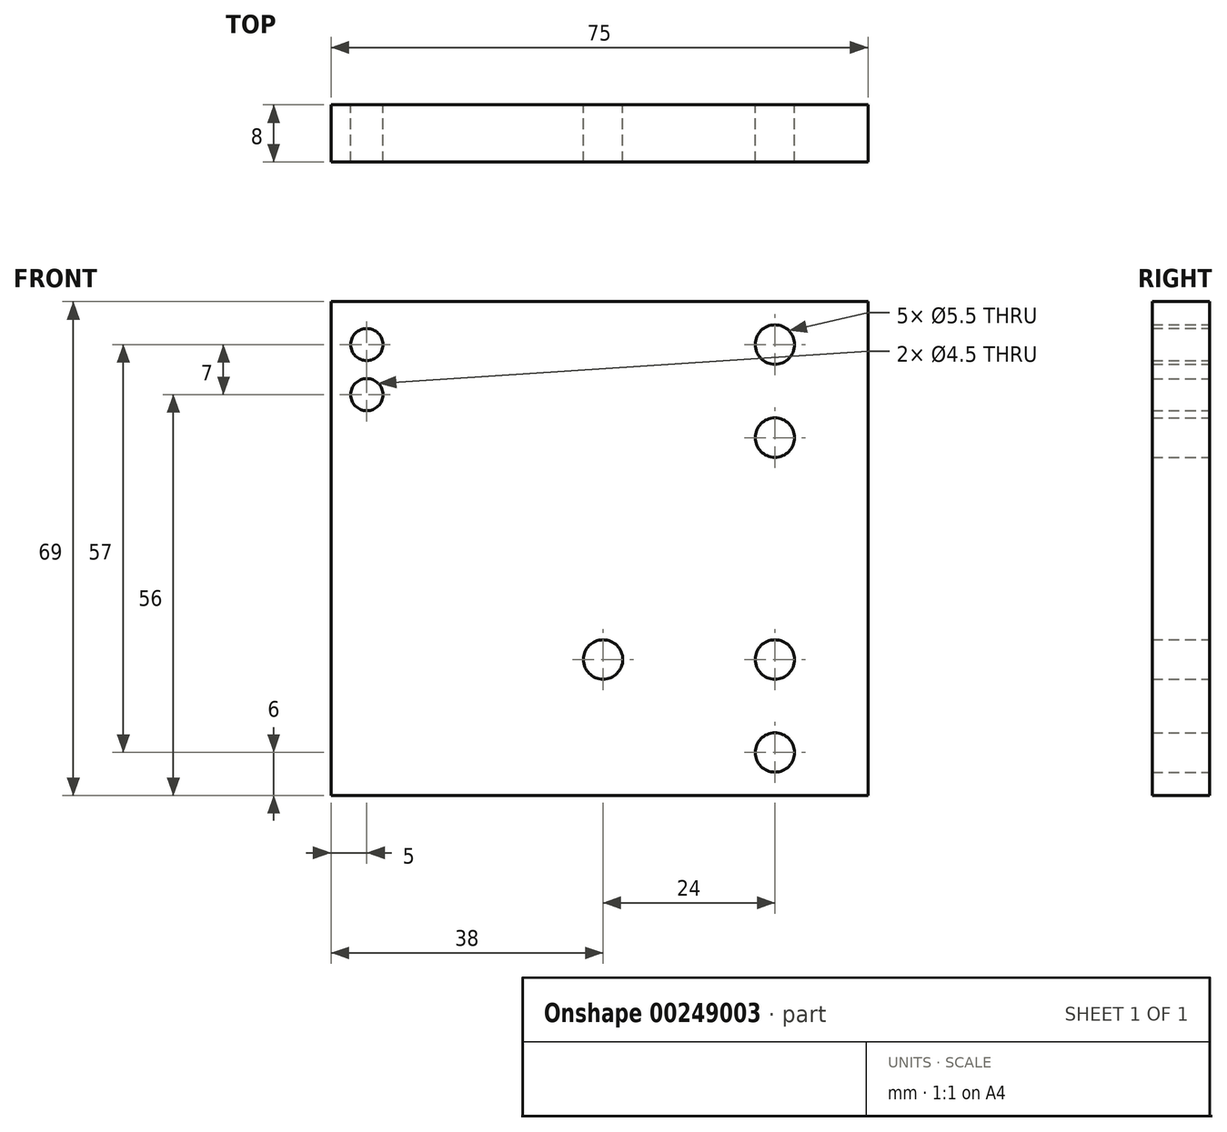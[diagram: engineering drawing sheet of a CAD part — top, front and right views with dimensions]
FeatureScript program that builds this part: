
annotation { "Feature Type Name" : "Feature", "Feature Type Description" : "" }
export const myFeature = defineFeature(function(context is Context, id is Id, definition is map)
    precondition{}
    {
        {
            var Q0;
            Q0=qCreatedBy(makeId("Front.planeOp"),FACE);
            var sketch = newSketch(context, id + "F0", { "sketchPlane" : qUnion([Q0])});
            skLineSegment(sketch, "E0.bottom", {"start": v(37.5, -34.5) * mm, "end": v(-37.5, -34.5) * mm});
            skLineSegment(sketch, "E0.top", {"start": v(37.5, 34.5) * mm, "end": v(-37.5, 34.5) * mm});
            skLineSegment(sketch, "E0.left", {"start": v(37.5, -34.5) * mm, "end": v(37.5, 34.5) * mm});
            skLineSegment(sketch, "E0.right", {"start": v(-37.5, -34.5) * mm, "end": v(-37.5, 34.5) * mm});
            skPoint(sketch, "E0.middle", {"position": v(0, 0) * mm});
            skCircle(sketch, "E1", {"center": v(24.5, -28.5) * mm, "radius": 2.75 * mm});
            skCircle(sketch, "E2", {"center": v(24.5, -15.5) * mm, "radius": 2.75 * mm});
            skCircle(sketch, "E3", {"center": v(24.5, 15.5) * mm, "radius": 2.75 * mm});
            skCircle(sketch, "E4", {"center": v(24.5, 28.5) * mm, "radius": 2.75 * mm});
            skCircle(sketch, "E5", {"center": v(-32.5, 28.5) * mm, "radius": 2.25 * mm});
            skCircle(sketch, "E6", {"center": v(-32.5, 21.5) * mm, "radius": 2.25 * mm});
            skPoint(sketch, "E7", {"position": v(0.5, -15.5) * mm});
            skSolve(sketch);
        }
        {
            var Q0;
            Q0=makeQuery(id+"F0.imprint","IMPRINT",FACE,{"disambiguationData":[TD([[makeQuery(id+"F0.imprint","IMPRINT",EDGE,{"derivedFrom":sQuery(id+"F0.wireOp",EDGE,"E0.bottom")}),-1.0]])]});
            extrude(context, id + "F1", {"entities" : qUnion([Q0]), "depth" : 8 * mm});
        }
        {
            var Q0;
            Q0=sQuery(id+"F0.wireOp",VERTEX,"E7");
            var Q1;
            Q1=makeQuery(id+"F1.opExtrude","SWEPT_BODY",BODY,{"disambiguationData":[OSD([sQuery(id+"F0.wireOp",EDGE,"E0.bottom"),sQuery(id+"F0.wireOp",EDGE,"E0.top"),sQuery(id+"F0.wireOp",EDGE,"E0.left"),sQuery(id+"F0.wireOp",EDGE,"E0.right"),sQuery(id+"F0.wireOp",EDGE,"E1"),sQuery(id+"F0.wireOp",EDGE,"E2"),sQuery(id+"F0.wireOp",EDGE,"E3"),sQuery(id+"F0.wireOp",EDGE,"E4"),sQuery(id+"F0.wireOp",EDGE,"E5"),sQuery(id+"F0.wireOp",EDGE,"E6")])]});
            hole(context, id + "F2", {"style" : HoleStyle.SIMPLE, "endStyle" : HoleEndStyle.THROUGH, "oppositeDirection" : true, "standardTappedOrClearance" : lookupTablePath({ "standard" : "ISO", "fit" : "Normal", "size" : "M5", "type" : "Clearance" }), "standardBlindInLast" : lookupTablePath({ "fit" : "Standard", "standard" : "ISO", "size" : "M5", "type" : "Clearance" }), "holeDiameter" : 5.5 * mm, "tappedDepth" : 12 * mm, "tapClearance" : 3, "startFromSketch" : true, "locations" : qUnion([Q0]), "scope" : qUnion([Q1])});
        }
    });
